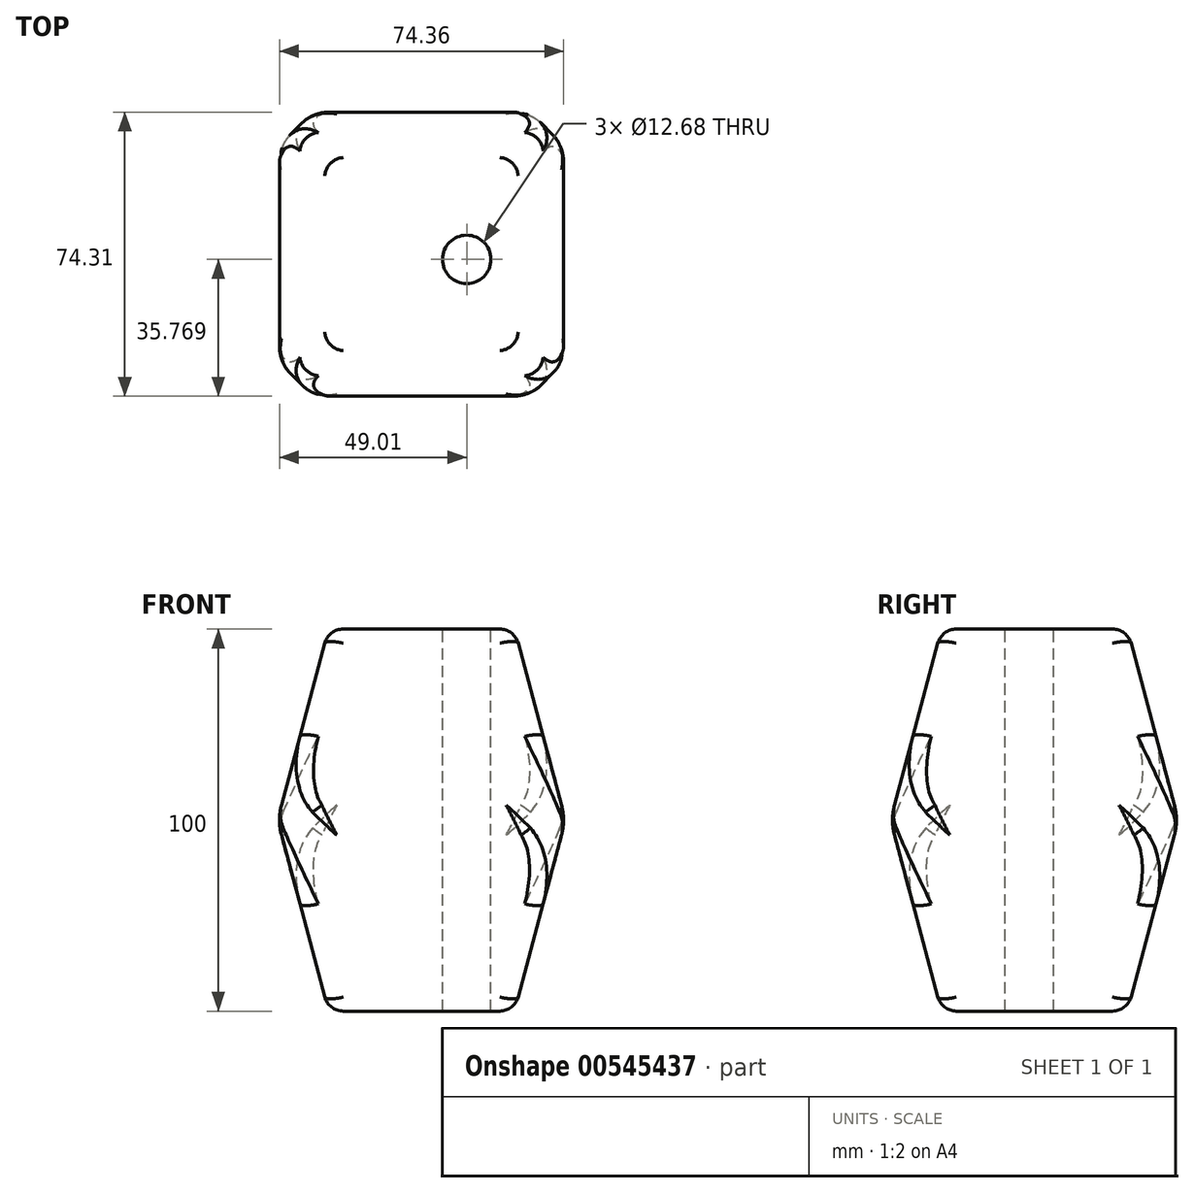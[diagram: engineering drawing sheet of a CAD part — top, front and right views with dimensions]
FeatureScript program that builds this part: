
annotation { "Feature Type Name" : "Feature", "Feature Type Description" : "" }
export const myFeature = defineFeature(function(context is Context, id is Id, definition is map)
    precondition{}
    {
        {
            var Q0;
            Q0=qCreatedBy(makeId("Top.planeOp"),FACE);
            var sketch = newSketch(context, id + "F0", { "sketchPlane" : qUnion([Q0])});
            skLineSegment(sketch, "E0.bottom", {"start": v(0, 0) * mm, "end": v(75.42, 0) * mm});
            skLineSegment(sketch, "E0.top", {"start": v(0, 75.37) * mm, "end": v(75.42, 75.37) * mm});
            skLineSegment(sketch, "E0.left", {"start": v(0, 0) * mm, "end": v(0, 75.37) * mm});
            skLineSegment(sketch, "E0.right", {"start": v(75.42, 0) * mm, "end": v(75.42, 75.37) * mm});
            skSolve(sketch);
        }
        {
            var Q0;
            Q0=makeQuery(id+"F0.imprint","IMPRINT",FACE,{"disambiguationData":[TD([[makeQuery(id+"F0.imprint","IMPRINT",EDGE,{"derivedFrom":sQuery(id+"F0.wireOp",EDGE,"E0.bottom")}),1.0]])]});
            extrude(context, id + "F1", {"entities" : qUnion([Q0]), "endBound" : BoundingType.SYMMETRIC, "depth" : 100 * mm, "offsetDistance" : 25 * mm, "hasDraft" : true, "draftAngle" : 15 * degree, "draftPullDirection" : true});
        }
        {
            var Q0;
            Q0=makeQuery(id+"F1.opExtrude","CAP_EDGE",EDGE,{"disambiguationData":[OSD([sQuery(id+"F0.wireOp",EDGE,"E0.left")])],"isStart":false});
            var Q1;
            Q1=makeQuery(id+"F1.opExtrude","CAP_EDGE",EDGE,{"disambiguationData":[OSD([sQuery(id+"F0.wireOp",EDGE,"E0.top")])],"isStart":false});
            var Q2;
            Q2=makeQuery(id+"F1.opExtrude","CAP_EDGE",EDGE,{"disambiguationData":[OSD([sQuery(id+"F0.wireOp",EDGE,"E0.right")])],"isStart":false});
            var Q3;
            Q3=makeQuery(id+"F1.opExtrude","CAP_EDGE",EDGE,{"disambiguationData":[OSD([sQuery(id+"F0.wireOp",EDGE,"E0.bottom")])],"isStart":false});
            fillet(context, id + "F2", {"entities" : qUnion([Q0, Q1, Q2, Q3]), "radius" : 5 * mm, "tangentPropagation" : true, "allowEdgeOverflow" : false});
        }
        {
            var Q0;
            Q0=makeQuery(id+"F1.opExtrude","CAP_EDGE",EDGE,{"disambiguationData":[OSD([sQuery(id+"F0.wireOp",EDGE,"E0.left")])],"isStart":true});
            var Q1;
            Q1=makeQuery(id+"F1.opExtrude","CAP_EDGE",EDGE,{"disambiguationData":[OSD([sQuery(id+"F0.wireOp",EDGE,"E0.bottom")])],"isStart":true});
            var Q2;
            Q2=makeQuery(id+"F1.opExtrude","CAP_EDGE",EDGE,{"disambiguationData":[OSD([sQuery(id+"F0.wireOp",EDGE,"E0.right")])],"isStart":true});
            var Q3;
            Q3=makeQuery(id+"F1.opExtrude","CAP_EDGE",EDGE,{"disambiguationData":[OSD([sQuery(id+"F0.wireOp",EDGE,"E0.top")])],"isStart":true});
            fillet(context, id + "F3", {"entities" : qUnion([Q0, Q1, Q2, Q3]), "radius" : 5 * mm, "tangentPropagation" : true, "allowEdgeOverflow" : false});
        }
        {
            var Q0;
            Q0=makeQuery(id+"F1.*.split.splitOp","SPLIT",EDGE,{"derivedFrom":makeQuery(id+"F1.opExtrude","SWEPT_EDGE",EDGE,{"disambiguationData":[OSD([sQuery(id+"F0.wireOp",EDGE,"E0.bottom"),sQuery(id+"F0.wireOp",EDGE,"E0.left")])]}),"isFromBackBody":true});
            var Q1;
            Q1=makeQuery(id+"F1.*.split.splitOp","SPLIT",EDGE,{"derivedFrom":makeQuery(id+"F1.opExtrude","SWEPT_EDGE",EDGE,{"disambiguationData":[OSD([sQuery(id+"F0.wireOp",EDGE,"E0.top"),sQuery(id+"F0.wireOp",EDGE,"E0.left")])]}),"isFromBackBody":true});
            var Q2;
            Q2=makeQuery(id+"F1.*.split.splitOp","SPLIT",EDGE,{"derivedFrom":makeQuery(id+"F1.opExtrude","SWEPT_EDGE",EDGE,{"disambiguationData":[OSD([sQuery(id+"F0.wireOp",EDGE,"E0.top"),sQuery(id+"F0.wireOp",EDGE,"E0.right")])]}),"isFromBackBody":true});
            var Q3;
            Q3=makeQuery(id+"F1.*.split.splitOp","SPLIT",EDGE,{"derivedFrom":makeQuery(id+"F1.opExtrude","SWEPT_EDGE",EDGE,{"disambiguationData":[OSD([sQuery(id+"F0.wireOp",EDGE,"E0.bottom"),sQuery(id+"F0.wireOp",EDGE,"E0.left")])]})});
            var Q4;
            Q4=makeQuery(id+"F1.*.split.splitOp","SPLIT",EDGE,{"derivedFrom":makeQuery(id+"F1.opExtrude","SWEPT_EDGE",EDGE,{"disambiguationData":[OSD([sQuery(id+"F0.wireOp",EDGE,"E0.top"),sQuery(id+"F0.wireOp",EDGE,"E0.right")])]})});
            var Q5;
            Q5=makeQuery(id+"F1.*.split.splitOp","SPLIT",EDGE,{"derivedFrom":makeQuery(id+"F1.opExtrude","SWEPT_EDGE",EDGE,{"disambiguationData":[OSD([sQuery(id+"F0.wireOp",EDGE,"E0.top"),sQuery(id+"F0.wireOp",EDGE,"E0.left")])]})});
            var Q6;
            Q6=makeQuery(id+"F1.*.split.splitOp","SPLIT",EDGE,{"derivedFrom":makeQuery(id+"F1.opExtrude","SWEPT_EDGE",EDGE,{"disambiguationData":[OSD([sQuery(id+"F0.wireOp",EDGE,"E0.bottom"),sQuery(id+"F0.wireOp",EDGE,"E0.right")])]}),"isFromBackBody":true});
            var Q7;
            Q7=makeQuery(id+"F1.*.split.splitOp","SPLIT",EDGE,{"derivedFrom":makeQuery(id+"F1.opExtrude","SWEPT_EDGE",EDGE,{"disambiguationData":[OSD([sQuery(id+"F0.wireOp",EDGE,"E0.bottom"),sQuery(id+"F0.wireOp",EDGE,"E0.right")])]})});
            fillet(context, id + "F4", {"entities" : qUnion([Q0, Q1, Q2, Q3, Q4, Q5, Q6, Q7]), "radius" : 5 * mm, "tangentPropagation" : true, "allowEdgeOverflow" : false});
        }
        {
            var Q0;
            {var subQ0=sQuery(id+"F0.wireOp",EDGE,"E0.right");var subQ1=sQuery(id+"F0.wireOp",EDGE,"E0.bottom");Q0=makeQuery(id+"F4.opFillet","BLEND_FACE",FACE,{"disambiguationData":[OSD([subQ1,subQ0]),TDD([makeQuery(id+"F1.*.split.splitOp","SPLIT",EDGE,{"derivedFrom":makeQuery(id+"F1.opExtrude","SWEPT_EDGE",EDGE,{"disambiguationData":[OSD([subQ1,subQ0])]})})])]});}
            var Q1;
            Q1=makeQuery(id+"F1.*.split.splitOp","SPLIT",FACE,{"derivedFrom":makeQuery(id+"F1.opExtrude","SWEPT_FACE",FACE,{"disambiguationData":[OSD([sQuery(id+"F0.wireOp",EDGE,"E0.right")])]})});
            var Q2;
            Q2=makeQuery(id+"F1.*.split.splitOp","SPLIT",FACE,{"derivedFrom":makeQuery(id+"F1.opExtrude","SWEPT_FACE",FACE,{"disambiguationData":[OSD([sQuery(id+"F0.wireOp",EDGE,"E0.right")])]}),"isFromBackBody":true});
            var Q3;
            {var subQ0=sQuery(id+"F0.wireOp",EDGE,"E0.right");var subQ1=sQuery(id+"F0.wireOp",EDGE,"E0.bottom");Q3=makeQuery(id+"F4.opFillet","BLEND_FACE",FACE,{"disambiguationData":[OSD([subQ1,subQ0]),TDD([makeQuery(id+"F1.*.split.splitOp","SPLIT",EDGE,{"derivedFrom":makeQuery(id+"F1.opExtrude","SWEPT_EDGE",EDGE,{"disambiguationData":[OSD([subQ1,subQ0])]}),"isFromBackBody":true})])]});}
            var Q4;
            Q4=makeQuery(id+"F1.*.split.splitOp","SPLIT",FACE,{"derivedFrom":makeQuery(id+"F1.opExtrude","SWEPT_FACE",FACE,{"disambiguationData":[OSD([sQuery(id+"F0.wireOp",EDGE,"E0.bottom")])]}),"isFromBackBody":true});
            var Q5;
            Q5=makeQuery(id+"F1.*.split.splitOp","SPLIT",FACE,{"derivedFrom":makeQuery(id+"F1.opExtrude","SWEPT_FACE",FACE,{"disambiguationData":[OSD([sQuery(id+"F0.wireOp",EDGE,"E0.bottom")])]})});
            var Q6;
            {var subQ0=sQuery(id+"F0.wireOp",EDGE,"E0.right");var subQ1=sQuery(id+"F0.wireOp",EDGE,"E0.top");Q6=makeQuery(id+"F4.opFillet","BLEND_FACE",FACE,{"disambiguationData":[OSD([subQ1,subQ0]),TDD([makeQuery(id+"F1.*.split.splitOp","SPLIT",EDGE,{"derivedFrom":makeQuery(id+"F1.opExtrude","SWEPT_EDGE",EDGE,{"disambiguationData":[OSD([subQ1,subQ0])]})})])]});}
            var Q7;
            {var subQ0=sQuery(id+"F0.wireOp",EDGE,"E0.right");var subQ1=sQuery(id+"F0.wireOp",EDGE,"E0.top");Q7=makeQuery(id+"F4.opFillet","BLEND_FACE",FACE,{"disambiguationData":[OSD([subQ1,subQ0]),TDD([makeQuery(id+"F1.*.split.splitOp","SPLIT",EDGE,{"derivedFrom":makeQuery(id+"F1.opExtrude","SWEPT_EDGE",EDGE,{"disambiguationData":[OSD([subQ1,subQ0])]}),"isFromBackBody":true})])]});}
            var Q8;
            {var subQ0=sQuery(id+"F0.wireOp",EDGE,"E0.left");var subQ1=sQuery(id+"F0.wireOp",EDGE,"E0.bottom");Q8=makeQuery(id+"F4.opFillet","BLEND_FACE",FACE,{"disambiguationData":[OSD([subQ1,subQ0]),TDD([makeQuery(id+"F1.*.split.splitOp","SPLIT",EDGE,{"derivedFrom":makeQuery(id+"F1.opExtrude","SWEPT_EDGE",EDGE,{"disambiguationData":[OSD([subQ1,subQ0])]})})])]});}
            var Q9;
            {var subQ0=sQuery(id+"F0.wireOp",EDGE,"E0.left");var subQ1=sQuery(id+"F0.wireOp",EDGE,"E0.bottom");Q9=makeQuery(id+"F4.opFillet","BLEND_FACE",FACE,{"disambiguationData":[OSD([subQ1,subQ0]),TDD([makeQuery(id+"F1.*.split.splitOp","SPLIT",EDGE,{"derivedFrom":makeQuery(id+"F1.opExtrude","SWEPT_EDGE",EDGE,{"disambiguationData":[OSD([subQ1,subQ0])]}),"isFromBackBody":true})])]});}
            var Q10;
            Q10=makeQuery(id+"F1.*.split.splitOp","SPLIT",FACE,{"derivedFrom":makeQuery(id+"F1.opExtrude","SWEPT_FACE",FACE,{"disambiguationData":[OSD([sQuery(id+"F0.wireOp",EDGE,"E0.left")])]})});
            var Q11;
            Q11=makeQuery(id+"F1.*.split.splitOp","SPLIT",FACE,{"derivedFrom":makeQuery(id+"F1.opExtrude","SWEPT_FACE",FACE,{"disambiguationData":[OSD([sQuery(id+"F0.wireOp",EDGE,"E0.left")])]}),"isFromBackBody":true});
            var Q12;
            Q12=makeQuery(id+"F1.*.split.splitOp","SPLIT",FACE,{"derivedFrom":makeQuery(id+"F1.opExtrude","SWEPT_FACE",FACE,{"disambiguationData":[OSD([sQuery(id+"F0.wireOp",EDGE,"E0.top")])]})});
            var Q13;
            {var subQ0=sQuery(id+"F0.wireOp",EDGE,"E0.left");var subQ1=sQuery(id+"F0.wireOp",EDGE,"E0.top");Q13=makeQuery(id+"F4.opFillet","BLEND_FACE",FACE,{"disambiguationData":[OSD([subQ1,subQ0]),TDD([makeQuery(id+"F1.*.split.splitOp","SPLIT",EDGE,{"derivedFrom":makeQuery(id+"F1.opExtrude","SWEPT_EDGE",EDGE,{"disambiguationData":[OSD([subQ1,subQ0])]})})])]});}
            var Q14;
            {var subQ0=sQuery(id+"F0.wireOp",EDGE,"E0.left");var subQ1=sQuery(id+"F0.wireOp",EDGE,"E0.top");Q14=makeQuery(id+"F4.opFillet","BLEND_FACE",FACE,{"disambiguationData":[OSD([subQ1,subQ0]),TDD([makeQuery(id+"F1.*.split.splitOp","SPLIT",EDGE,{"derivedFrom":makeQuery(id+"F1.opExtrude","SWEPT_EDGE",EDGE,{"disambiguationData":[OSD([subQ1,subQ0])]}),"isFromBackBody":true})])]});}
            var Q15;
            Q15=makeQuery(id+"F1.*.split.splitOp","SPLIT",FACE,{"derivedFrom":makeQuery(id+"F1.opExtrude","SWEPT_FACE",FACE,{"disambiguationData":[OSD([sQuery(id+"F0.wireOp",EDGE,"E0.top")])]}),"isFromBackBody":true});
            fillet(context, id + "F5", {"entities" : qUnion([Q0, Q1, Q2, Q3, Q4, Q5, Q6, Q7, Q8, Q9, Q10, Q11, Q12, Q13, Q14, Q15]), "radius" : 15 * mm, "tangentPropagation" : true, "allowEdgeOverflow" : false});
        }
        {
            var Q0;
            Q0=makeQuery(id+"F1.opExtrude","CAP_FACE",FACE,{"disambiguationData":[OSD([sQuery(id+"F0.wireOp",EDGE,"E0.bottom"),sQuery(id+"F0.wireOp",EDGE,"E0.top"),sQuery(id+"F0.wireOp",EDGE,"E0.left"),sQuery(id+"F0.wireOp",EDGE,"E0.right")])],"isStart":false});
            var sketch = newSketch(context, id + "F6", { "sketchPlane" : qUnion([Q0])});
            skCircle(sketch, "E1", {"center": v(49.54, 36.3) * mm, "radius": 6.34 * mm});
            skSolve(sketch);
        }
        {
            var Q0;
            Q0 = qSketchRegion(id + "F6", true);
            var Q1;
            Q1=makeQuery(id+"F6.imprint","IMPRINT",FACE,{"disambiguationData":[TD([[makeQuery(id+"F6.imprint","IMPRINT",EDGE,{"derivedFrom":sQuery(id+"F6.wireOp",EDGE,"E1")}),1.0]])]});
            extrude(context, id + "F7", {"entities" : qUnion([Q0, Q1]), "operationType" : NewBodyOperationType.REMOVE, "oppositeDirection" : true, "depth" : 100 * mm, "offsetDistance" : 25 * mm});
        }
    });
